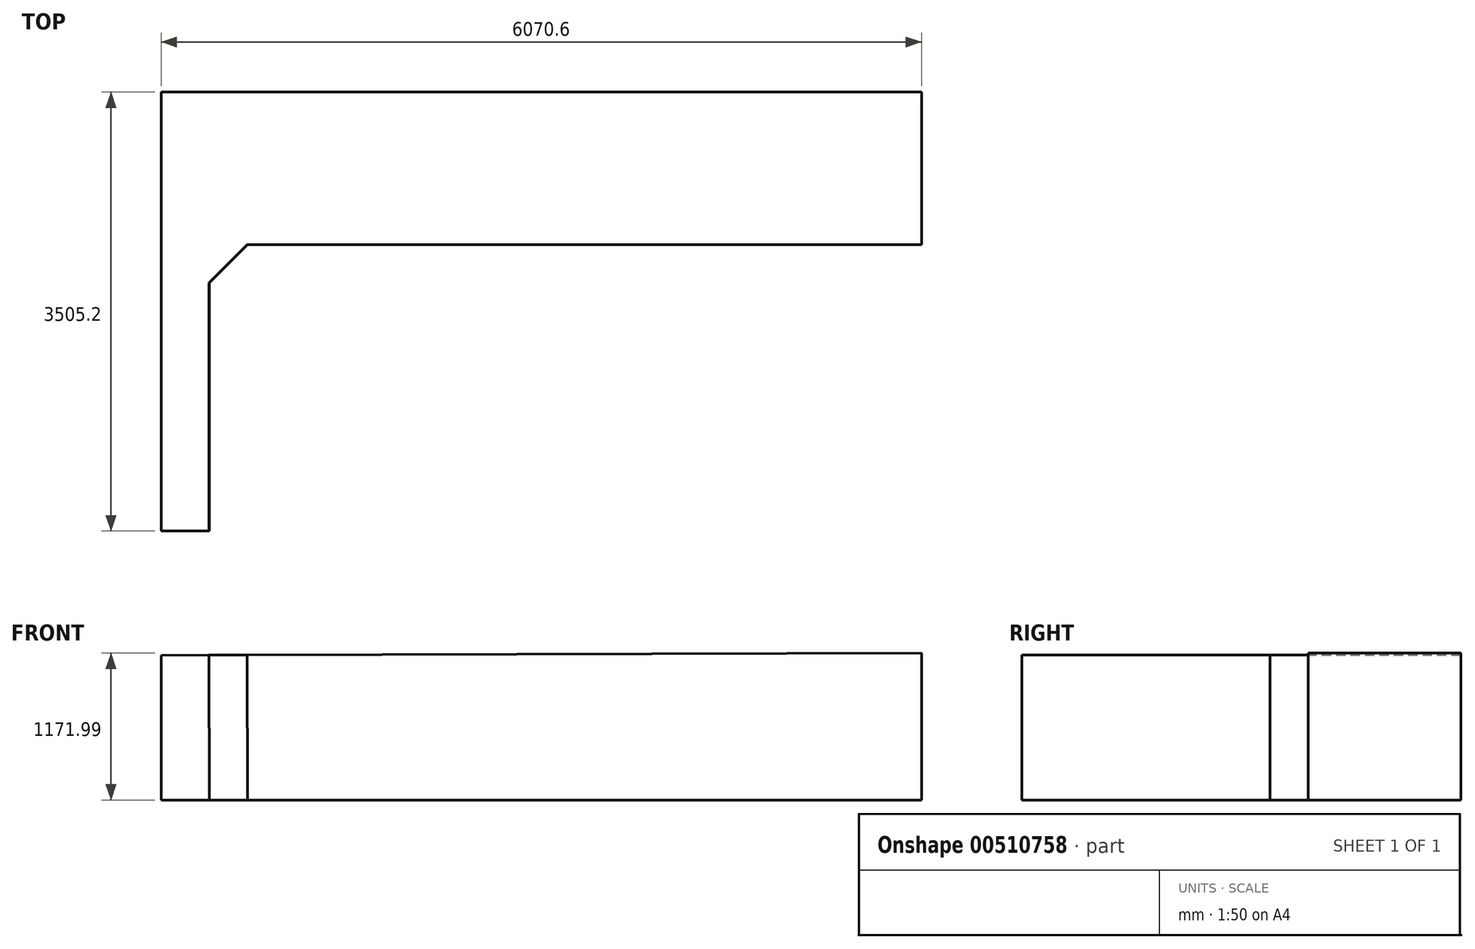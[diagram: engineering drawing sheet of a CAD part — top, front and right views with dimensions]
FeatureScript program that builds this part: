
annotation { "Feature Type Name" : "Feature", "Feature Type Description" : "" }
export const myFeature = defineFeature(function(context is Context, id is Id, definition is map)
    precondition{}
    {
        {
            var Q0;
            Q0=qCreatedBy(makeId("Right.planeOp"),FACE);
            var sketch = newSketch(context, id + "F0", { "sketchPlane" : qUnion([Q0])});
            skLineSegment(sketch, "E0.bottom", {"start": v(0, 295.66) * mm, "end": v(-3505.2, 295.66) * mm});
            skLineSegment(sketch, "E0.top", {"start": v(0, 1484.38) * mm, "end": v(-3505.2, 1484.38) * mm});
            skLineSegment(sketch, "E0.left", {"start": v(0, 295.66) * mm, "end": v(0, 1484.38) * mm});
            skLineSegment(sketch, "E0.right", {"start": v(-3505.2, 295.66) * mm, "end": v(-3505.2, 1484.38) * mm});
            skSolve(sketch);
        }
        {
            var Q0;
            Q0=qCreatedBy(makeId("Right.planeOp"),FACE);
            cPlane(context, id + "F1", {"entities" : qUnion([Q0]), "cplaneType" : CPlaneType.OFFSET, "offset" : 12115.8 * mm, "oppositeDirection" : true, "width" : 152.4 * mm, "height" : 152.4 * mm});
        }
        {
            var Q0;
            Q0=qCreatedBy(id+"F1.planeOp",FACE);
            var sketch = newSketch(context, id + "F2", { "sketchPlane" : qUnion([Q0])});
            skLineSegment(sketch, "E1.bottom", {"start": v(0, 295.66) * mm, "end": v(-3505.2, 295.66) * mm});
            skLineSegment(sketch, "E1.top", {"start": v(0, 1450.85) * mm, "end": v(-3505.2, 1450.85) * mm});
            skLineSegment(sketch, "E1.left", {"start": v(0, 295.66) * mm, "end": v(0, 1450.85) * mm});
            skLineSegment(sketch, "E1.right", {"start": v(-3505.2, 295.66) * mm, "end": v(-3505.2, 1450.85) * mm});
            skSolve(sketch);
        }
        {
            var Q0;
            Q0=makeQuery(id+"F0.imprint","IMPRINT",FACE,{"disambiguationData":[TD([[makeQuery(id+"F0.imprint","IMPRINT",EDGE,{"derivedFrom":sQuery(id+"F0.wireOp",EDGE,"E0.bottom")}),-1.0]])]});
            var Q1;
            Q1=makeQuery(id+"F2.imprint","IMPRINT",FACE,{"disambiguationData":[TD([[makeQuery(id+"F2.imprint","IMPRINT",EDGE,{"derivedFrom":sQuery(id+"F2.wireOp",EDGE,"E1.bottom")}),-1.0]])]});
            loft(context, id + "F3", {"sheetProfilesArray" : [{ "sheetProfileEntities" : qUnion([Q0]) }, { "sheetProfileEntities" : qUnion([Q1]) }]});
        }
        {
            var Q0;
            Q0=makeQuery(id+"F3.opLoft","SWEPT_FACE",FACE,{"disambiguationData":[OSD([sQuery(id+"F0.wireOp",EDGE,"E0.top"),sQuery(id+"F0.wireOp",EDGE,"E0.left"),sQuery(id+"F0.wireOp",EDGE,"E0.right"),sQuery(id+"F2.wireOp",EDGE,"E1.top"),sQuery(id+"F2.wireOp",EDGE,"E1.left"),sQuery(id+"F2.wireOp",EDGE,"E1.right")])]});
            var sketch = newSketch(context, id + "F4", { "sketchPlane" : qUnion([Q0])});
            skLineSegment(sketch, "E2", {"start": v(-11730.74, -3505.2) * mm, "end": v(-11730.74, -1524) * mm});
            skLineSegment(sketch, "E3", {"start": v(-11730.74, -1524) * mm, "end": v(-11425.94, -1219.2) * mm});
            skLineSegment(sketch, "E4", {"start": v(-11425.94, -1219.2) * mm, "end": v(-681.7, -1219.2) * mm});
            skLineSegment(sketch, "E5", {"start": v(-681.7, -1219.2) * mm, "end": v(-376.9, -1524) * mm});
            skLineSegment(sketch, "E6", {"start": v(-376.9, -1524) * mm, "end": v(-376.9, -3505.2) * mm});
            skLineSegment(sketch, "E7", {"start": v(-376.9, -3505.2) * mm, "end": v(-11730.74, -3505.2) * mm});
            skSolve(sketch);
        }
        {
            var Q0;
            Q0=qSketchRegion(id+"F4",true);
            extrude(context, id + "F5", {"entities" : qUnion([Q0]), "operationType" : NewBodyOperationType.REMOVE, "endBound" : BoundingType.UP_TO_NEXT, "oppositeDirection" : true, "depth" : 30.48 * mm});
        }
        {
            var Q0;
            Q0=qCreatedBy(makeId("Right.planeOp"),FACE);
            cPlane(context, id + "F6", {"entities" : qUnion([Q0]), "cplaneType" : CPlaneType.OFFSET, "offset" : 6045.2 * mm, "oppositeDirection" : true, "width" : 152.4 * mm, "height" : 152.4 * mm});
        }
        {
            var Q0;
            Q0=qCreatedBy(id+"F6.planeOp",FACE);
            var sketch = newSketch(context, id + "F7", { "sketchPlane" : qUnion([Q0])});
            skLineSegment(sketch, "E8.bottom", {"start": v(0, 0) * mm, "end": v(-3505.2, 0) * mm});
            skLineSegment(sketch, "E8.top", {"start": v(0, 1828.8) * mm, "end": v(-3505.2, 1828.8) * mm});
            skLineSegment(sketch, "E8.left", {"start": v(0, 0) * mm, "end": v(0, 1828.8) * mm});
            skLineSegment(sketch, "E8.right", {"start": v(-3505.2, 0) * mm, "end": v(-3505.2, 1828.8) * mm});
            skSolve(sketch);
        }
        {
            var Q0;
            Q0=qSketchRegion(id+"F7",true);
            extrude(context, id + "F8", {"entities" : qUnion([Q0]), "operationType" : NewBodyOperationType.REMOVE, "endBound" : BoundingType.UP_TO_NEXT, "depth" : 30.48 * mm});
        }
    });
